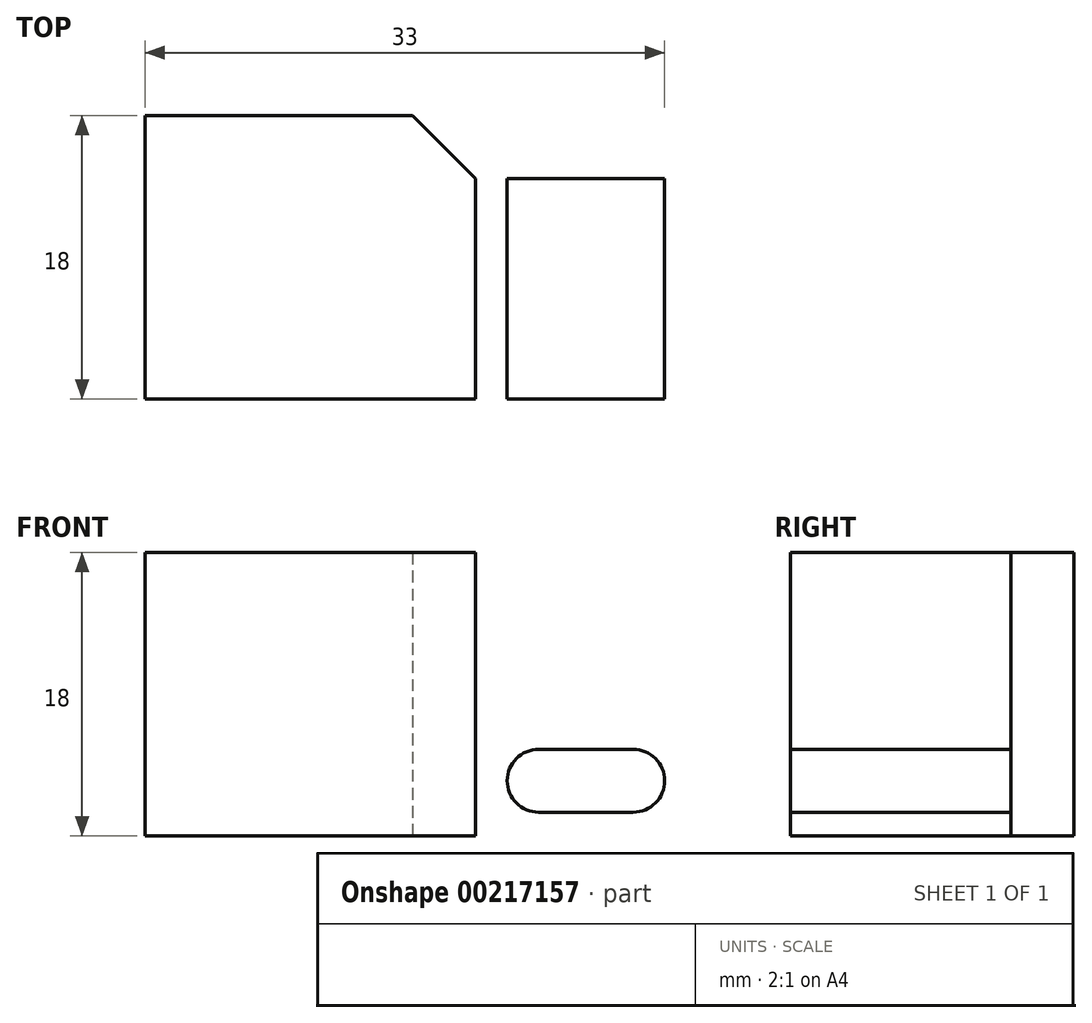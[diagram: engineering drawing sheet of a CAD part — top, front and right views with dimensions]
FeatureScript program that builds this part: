
annotation { "Feature Type Name" : "Feature", "Feature Type Description" : "" }
export const myFeature = defineFeature(function(context is Context, id is Id, definition is map)
    precondition{}
    {
        {
            var Q0;
            Q0=qCreatedBy(makeId("Top.planeOp"),FACE);
            var sketch = newSketch(context, id + "F0", { "sketchPlane" : qUnion([Q0])});
            skLineSegment(sketch, "E0", {"start": v(0, 0) * mm, "end": v(0, 18) * mm});
            skLineSegment(sketch, "E1", {"start": v(0, 18) * mm, "end": v(17, 18) * mm});
            skLineSegment(sketch, "E2", {"start": v(17, 18) * mm, "end": v(21, 14) * mm});
            skLineSegment(sketch, "E3", {"start": v(21, 14) * mm, "end": v(34, 14) * mm});
            skLineSegment(sketch, "E4", {"start": v(34, 14) * mm, "end": v(34, 0) * mm});
            skLineSegment(sketch, "E5", {"start": v(34, 0) * mm, "end": v(0, 0) * mm});
            skSolve(sketch);
        }
        {
            var Q0;
            Q0=makeQuery(id+"F0.imprint","IMPRINT",FACE,{"disambiguationData":[TD([[makeQuery(id+"F0.imprint","IMPRINT",EDGE,{"derivedFrom":sQuery(id+"F0.wireOp",EDGE,"E0")}),-1.0]])]});
            extrude(context, id + "F1", {"entities" : qUnion([Q0]), "depth" : 18 * mm});
        }
        {
            var Q0;
            Q0=qCreatedBy(makeId("Front.planeOp"),FACE);
            var sketch = newSketch(context, id + "F2", { "sketchPlane" : qUnion([Q0])});
            skLineSegment(sketch, "E6", {"start": v(27.36, 10) * mm, "end": v(50.1, 10) * mm, "construction": true});
            skLineSegment(sketch, "E7.0.0", {"start": v(34, 0) * mm, "end": v(21, 0) * mm});
            skLineSegment(sketch, "E7.0.1", {"start": v(21, 0) * mm, "end": v(21, 18) * mm});
            skLineSegment(sketch, "E7.0.2", {"start": v(21, 18) * mm, "end": v(34, 18) * mm});
            skLineSegment(sketch, "E7.0.3", {"start": v(34, 18) * mm, "end": v(34, 0) * mm});
            skLineSegment(sketch, "E8", {"start": v(34, 9) * mm, "end": v(-3.33, 9) * mm, "construction": true});
            skPoint(sketch, "E8.endSnap0", {"position": v(21, 9) * mm});
            skLineSegment(sketch, "E9.0.0", {"start": v(17, 0) * mm, "end": v(0, 0) * mm});
            skLineSegment(sketch, "E9.0.1", {"start": v(0, 0) * mm, "end": v(0, 18) * mm});
            skLineSegment(sketch, "E9.0.2", {"start": v(0, 18) * mm, "end": v(17, 18) * mm});
            skLineSegment(sketch, "E9.0.3", {"start": v(17, 18) * mm, "end": v(17, 0) * mm});
            skLineSegment(sketch, "E10.MirrorCS", {"start": v(34, 20) * mm, "end": v(-3.33, 20) * mm, "construction": true});
            skLineSegment(sketch, "E11.bottom", {"start": v(31, 16.5) * mm, "end": v(25, 16.5) * mm});
            skLineSegment(sketch, "E11.top", {"start": v(31, 12.5) * mm, "end": v(25, 12.5) * mm});
            skLineSegment(sketch, "E11.left", {"start": v(33, 14.5) * mm, "end": v(33, 14.5) * mm});
            skLineSegment(sketch, "E11.right", {"start": v(23, 14.5) * mm, "end": v(23, 14.5) * mm});
            skPoint(sketch, "E12.visualSharp", {"position": v(23, 16.5) * mm});
            skArc(sketch, "E12.filletArc", {"start": v(25, 16.5) * mm, "mid": v(23.59, 15.91) * mm, "end": v(23, 14.5) * mm});
            skPoint(sketch, "E13.visualSharp", {"position": v(23, 12.5) * mm});
            skArc(sketch, "E13.filletArc", {"start": v(23, 14.5) * mm, "mid": v(23.59, 13.09) * mm, "end": v(25, 12.5) * mm});
            skPoint(sketch, "E14.visualSharp", {"position": v(33, 12.5) * mm});
            skArc(sketch, "E14.filletArc", {"start": v(31, 12.5) * mm, "mid": v(32.41, 13.09) * mm, "end": v(33, 14.5) * mm});
            skPoint(sketch, "E15.visualSharp", {"position": v(33, 16.5) * mm});
            skArc(sketch, "E15.filletArc", {"start": v(33, 14.5) * mm, "mid": v(32.41, 15.91) * mm, "end": v(31, 16.5) * mm});
            skPoint(sketch, "E16.MirrorP", {"position": v(23, 1.5) * mm});
            skPoint(sketch, "E17.MirrorP", {"position": v(23, 5.5) * mm});
            skArc(sketch, "E18.MirrorCS", {"start": v(25, 1.5) * mm, "mid": v(23.59, 2.09) * mm, "end": v(23, 3.5) * mm});
            skArc(sketch, "E19.MirrorCS", {"start": v(23, 3.5) * mm, "mid": v(23.59, 4.91) * mm, "end": v(25, 5.5) * mm});
            skArc(sketch, "E20.MirrorCS", {"start": v(31, 5.5) * mm, "mid": v(32.41, 4.91) * mm, "end": v(33, 3.5) * mm});
            skLineSegment(sketch, "E21.MirrorCS", {"start": v(23, 3.5) * mm, "end": v(23, 3.5) * mm});
            skPoint(sketch, "E22.MirrorP", {"position": v(33, 1.5) * mm});
            skArc(sketch, "E23.MirrorCS", {"start": v(33, 3.5) * mm, "mid": v(32.41, 2.09) * mm, "end": v(31, 1.5) * mm});
            skPoint(sketch, "E24.MirrorP", {"position": v(33, 5.5) * mm});
            skLineSegment(sketch, "E25.MirrorCS", {"start": v(33, 3.5) * mm, "end": v(33, 3.5) * mm});
            skLineSegment(sketch, "E26.MirrorCS", {"start": v(31, 5.5) * mm, "end": v(25, 5.5) * mm});
            skLineSegment(sketch, "E27.MirrorCS", {"start": v(31, 1.5) * mm, "end": v(25, 1.5) * mm});
            skSolve(sketch);
        }
        {
            var Q0;
            Q0=makeQuery(id+"F2.imprint","IMPRINT",FACE,{"disambiguationData":[TD([[makeQuery(id+"F2.imprint","IMPRINT",EDGE,{"derivedFrom":sQuery(id+"F2.wireOp",EDGE,"E11.bottom")}),1.0]])]});
            var Q1;
            Q1=makeQuery(id+"F2.imprint","IMPRINT",FACE,{"disambiguationData":[TD([[makeQuery(id+"F2.imprint","IMPRINT",EDGE,{"derivedFrom":sQuery(id+"F2.wireOp",EDGE,"E18.MirrorCS")}),-1.0]])]});
            extrude(context, id + "F3", {"entities" : qUnion([Q0, Q1]), "operationType" : NewBodyOperationType.REMOVE, "oppositeDirection" : true, "depth" : 15 * mm});
        }
    });
